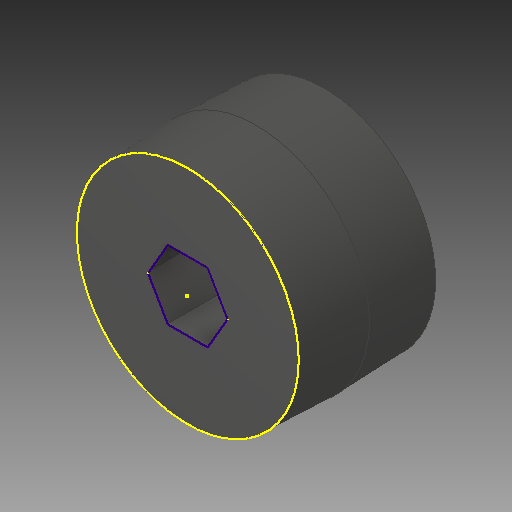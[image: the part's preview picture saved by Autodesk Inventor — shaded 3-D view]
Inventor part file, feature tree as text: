
AUTODESK INVENTOR PART (.ipt)
format: ipt  version: 2017 (Build 210142000, 142)  size: 684,544 bytes
history: native  units: in
note: dims shown in document units (in); Inventor stores cm internally (conversion verified against a paired STEP export)
features: sketch x1, projected_geometry x1, other x1
ambient origin geometry x8: Origin, YZ Plane, XZ Plane, XY Plane, X Axis, Y Axis, Z Axis, Center Point
bodies: Solid1 (feature_tree)
feature tree (3):
  sketch  "Sketch1"
  projected_geometry  "Projected Loop1"
  other  "_2in Wheel Intergrated Hub Design_-_CirPattern1_"
